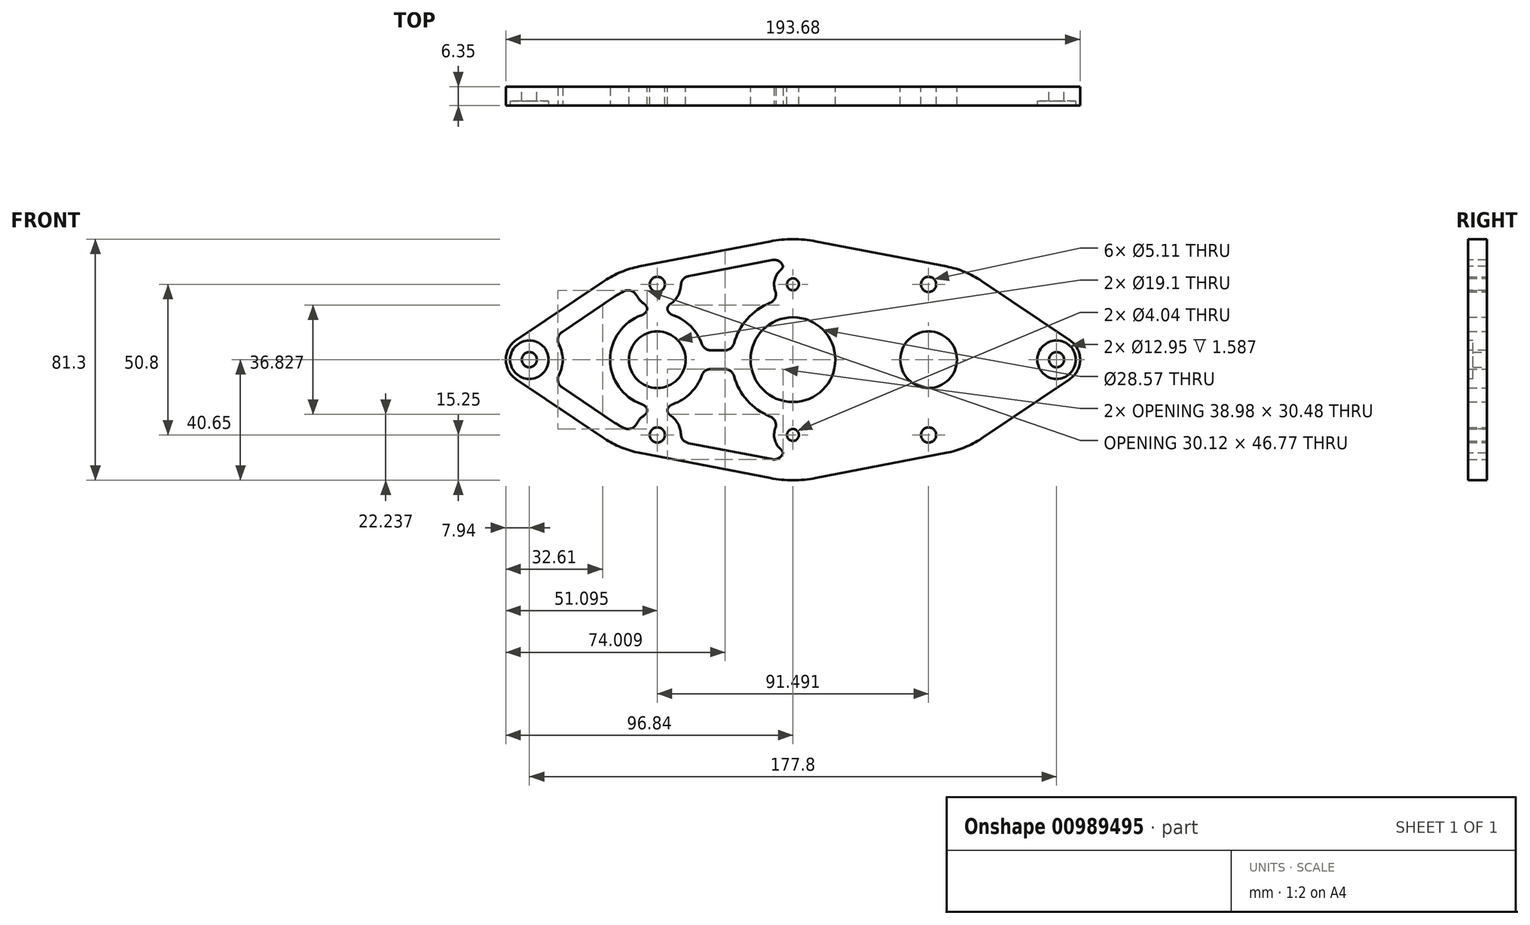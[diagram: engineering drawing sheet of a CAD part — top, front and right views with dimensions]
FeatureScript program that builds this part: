
annotation { "Feature Type Name" : "Feature", "Feature Type Description" : "" }
export const myFeature = defineFeature(function(context is Context, id is Id, definition is map)
    precondition{}
    {
        {
            var Q0;
            Q0=qCreatedBy(makeId("Front.planeOp"),FACE);
            var sketch = newSketch(context, id + "F0", { "sketchPlane" : qUnion([Q0])});
            skCircle(sketch, "E0", {"center": v(-45.75, 0) * mm, "radius": 32 * mm, "construction": true});
            skCircle(sketch, "E1", {"center": v(45.75, 0) * mm, "radius": 32 * mm, "construction": true});
            skLineSegment(sketch, "E2.bottom", {"start": v(-127, -25.4) * mm, "end": v(127, -25.4) * mm, "construction": true});
            skLineSegment(sketch, "E2.top", {"start": v(-127, 25.4) * mm, "end": v(127, 25.4) * mm, "construction": true});
            skLineSegment(sketch, "E2.left", {"start": v(-127, -25.4) * mm, "end": v(-127, 25.4) * mm, "construction": true});
            skLineSegment(sketch, "E2.right", {"start": v(127, -25.4) * mm, "end": v(127, 25.4) * mm, "construction": true});
            skPoint(sketch, "E2.middle", {"position": v(0, 0) * mm});
            skCircle(sketch, "E3", {"center": v(0, 0) * mm, "radius": 50.8 * mm, "construction": true});
            skPoint(sketch, "E3.centerSnap0", {"position": v(0, -25.4) * mm});
            skLineSegment(sketch, "E4", {"start": v(0, 0) * mm, "end": v(0, 0) * mm});
            skLineSegment(sketch, "E5", {"start": v(-45.75, 0) * mm, "end": v(45.75, 0) * mm, "construction": true});
            skCircle(sketch, "E6", {"center": v(-45.75, 0) * mm, "radius": 7.63 * mm, "construction": true});
            skCircle(sketch, "E7", {"center": v(0, 0) * mm, "radius": 38.11 * mm, "construction": true});
            skCircle(sketch, "E8", {"center": v(0, 0) * mm, "radius": 40.65 * mm, "construction": true});
            skCircle(sketch, "E9", {"center": v(-45.75, 0) * mm, "radius": 9.55 * mm});
            skCircle(sketch, "E10", {"center": v(45.75, 0) * mm, "radius": 9.55 * mm});
            skCircle(sketch, "E11", {"center": v(-114.3, 12.7) * mm, "radius": 2.55 * mm, "construction": true});
            skCircle(sketch, "E12.0.1.0", {"center": v(-114.3, -12.7) * mm, "radius": 2.55 * mm, "construction": true});
            skCircle(sketch, "E12.1.0.0", {"center": v(-88.9, 12.7) * mm, "radius": 2.55 * mm, "construction": true});
            skCircle(sketch, "E12.1.1.0", {"center": v(-88.9, -12.7) * mm, "radius": 2.55 * mm, "construction": true});
            skCircle(sketch, "E12.2.0.0", {"center": v(-63.5, 12.7) * mm, "radius": 2.55 * mm, "construction": true});
            skCircle(sketch, "E12.2.1.0", {"center": v(-63.5, -12.7) * mm, "radius": 2.55 * mm, "construction": true});
            skCircle(sketch, "E12.3.0.0", {"center": v(-38.1, 12.7) * mm, "radius": 2.55 * mm, "construction": true});
            skCircle(sketch, "E12.3.1.0", {"center": v(-38.1, -12.7) * mm, "radius": 2.55 * mm, "construction": true});
            skCircle(sketch, "E12.4.0.0", {"center": v(-12.7, 12.7) * mm, "radius": 2.55 * mm, "construction": true});
            skCircle(sketch, "E12.4.1.0", {"center": v(-12.7, -12.7) * mm, "radius": 2.55 * mm, "construction": true});
            skCircle(sketch, "E12.5.0.0", {"center": v(12.7, 12.7) * mm, "radius": 2.55 * mm, "construction": true});
            skCircle(sketch, "E12.5.1.0", {"center": v(12.7, -12.7) * mm, "radius": 2.55 * mm, "construction": true});
            skCircle(sketch, "E12.6.0.0", {"center": v(38.1, 12.7) * mm, "radius": 2.55 * mm, "construction": true});
            skCircle(sketch, "E12.6.1.0", {"center": v(38.1, -12.7) * mm, "radius": 2.55 * mm, "construction": true});
            skCircle(sketch, "E12.7.0.0", {"center": v(63.5, 12.7) * mm, "radius": 2.55 * mm, "construction": true});
            skCircle(sketch, "E12.7.1.0", {"center": v(63.5, -12.7) * mm, "radius": 2.55 * mm, "construction": true});
            skCircle(sketch, "E12.8.0.0", {"center": v(88.9, 12.7) * mm, "radius": 2.55 * mm, "construction": true});
            skCircle(sketch, "E12.8.1.0", {"center": v(88.9, -12.7) * mm, "radius": 2.55 * mm, "construction": true});
            skCircle(sketch, "E12.9.0.0", {"center": v(114.3, 12.7) * mm, "radius": 2.55 * mm, "construction": true});
            skCircle(sketch, "E12.9.1.0", {"center": v(114.3, -12.7) * mm, "radius": 2.55 * mm, "construction": true});
            skLineSegment(sketch, "E12.direction1", {"start": v(-114.3, 12.7) * mm, "end": v(-88.9, 12.7) * mm, "construction": true});
            skLineSegment(sketch, "E12.direction2", {"start": v(-114.3, 12.7) * mm, "end": v(-114.3, -12.7) * mm, "construction": true});
            skLineSegment(sketch, "E13", {"start": v(-45.75, -25.4) * mm, "end": v(-45.75, 0) * mm, "construction": true});
            skLineSegment(sketch, "E14", {"start": v(-45.75, 0) * mm, "end": v(-45.75, 25.4) * mm, "construction": true});
            skCircle(sketch, "E15", {"center": v(-45.75, 25.4) * mm, "radius": 2.55 * mm});
            skCircle(sketch, "E16", {"center": v(-45.75, -25.4) * mm, "radius": 2.55 * mm});
            skCircle(sketch, "E17.MirrorC", {"center": v(45.75, -25.4) * mm, "radius": 2.55 * mm});
            skLineSegment(sketch, "E18.MirrorCS", {"start": v(45.75, -25.4) * mm, "end": v(45.75, 0) * mm, "construction": true});
            skLineSegment(sketch, "E19.MirrorCS", {"start": v(45.75, 0) * mm, "end": v(45.75, 25.4) * mm, "construction": true});
            skCircle(sketch, "E20.MirrorC", {"center": v(45.75, 25.4) * mm, "radius": 2.55 * mm});
            skCircle(sketch, "E21", {"center": v(0, 0) * mm, "radius": 14.29 * mm});
            skCircle(sketch, "E22", {"center": v(0, 0) * mm, "radius": 15.88 * mm, "construction": true});
            skCircle(sketch, "E23", {"center": v(45.75, 0) * mm, "radius": 7.63 * mm, "construction": true});
            skArc(sketch, "E24", {"start": v(-7.69, 39.92) * mm, "mid": v(0, 40.65) * mm, "end": v(7.69, 39.92) * mm});
            skLineSegment(sketch, "E25", {"start": v(-7.69, 39.92) * mm, "end": v(-51.8, 31.43) * mm});
            skLineSegment(sketch, "E26", {"start": v(7.69, 39.92) * mm, "end": v(51.8, 31.43) * mm});
            skCircle(sketch, "E27", {"center": v(0, 0) * mm, "radius": 18.29 * mm, "construction": true});
            skCircle(sketch, "E28", {"center": v(-88.9, 0) * mm, "radius": 2.55 * mm});
            skCircle(sketch, "E29", {"center": v(88.9, 0) * mm, "radius": 2.55 * mm});
            skCircle(sketch, "E30", {"center": v(88.9, 0) * mm, "radius": 7.94 * mm, "construction": true});
            skCircle(sketch, "E31", {"center": v(-88.9, 0) * mm, "radius": 7.94 * mm, "construction": true});
            skLineSegment(sketch, "E32", {"start": v(63.6, 26.57) * mm, "end": v(93.33, 6.59) * mm});
            skArc(sketch, "E33", {"start": v(51.8, 31.43) * mm, "mid": v(57.94, 29.59) * mm, "end": v(63.6, 26.57) * mm});
            skArc(sketch, "E34", {"start": v(93.33, 6.59) * mm, "mid": v(96.84, 0) * mm, "end": v(93.33, -6.59) * mm});
            skArc(sketch, "E35", {"start": v(51.8, -31.43) * mm, "mid": v(57.94, -29.59) * mm, "end": v(63.6, -26.57) * mm});
            skLineSegment(sketch, "E36", {"start": v(63.6, -26.57) * mm, "end": v(93.33, -6.59) * mm});
            skArc(sketch, "E37", {"start": v(-93.33, 6.59) * mm, "mid": v(-96.84, 0) * mm, "end": v(-93.33, -6.59) * mm});
            skLineSegment(sketch, "E38", {"start": v(-93.33, -6.59) * mm, "end": v(-63.6, -26.57) * mm});
            skArc(sketch, "E39", {"start": v(-63.6, -26.57) * mm, "mid": v(-57.94, -29.59) * mm, "end": v(-51.8, -31.43) * mm});
            skArc(sketch, "E40", {"start": v(-51.8, 31.43) * mm, "mid": v(-57.94, 29.59) * mm, "end": v(-63.6, 26.57) * mm});
            skLineSegment(sketch, "E41", {"start": v(-63.6, 26.57) * mm, "end": v(-93.33, 6.59) * mm});
            skArc(sketch, "E42", {"start": v(-7.69, -39.92) * mm, "mid": v(0, -40.65) * mm, "end": v(7.69, -39.92) * mm});
            skLineSegment(sketch, "E43", {"start": v(7.69, -39.92) * mm, "end": v(51.8, -31.43) * mm});
            skLineSegment(sketch, "E44", {"start": v(-7.69, -39.92) * mm, "end": v(-51.8, -31.43) * mm});
            skCircle(sketch, "E45", {"center": v(0, 25.4) * mm, "radius": 2.02 * mm});
            skPoint(sketch, "E45.centerSnap0", {"position": v(0, 25.4) * mm});
            skCircle(sketch, "E46", {"center": v(0, -25.4) * mm, "radius": 2.02 * mm});
            skSolve(sketch);
        }
        {
            var Q0;
            Q0 = qSketchRegion(id + "F0", true);
            extrude(context, id + "F1", {"entities" : qUnion([Q0]), "depth" : 6.35 * mm, "offsetDistance" : 25.4 * mm});
        }
        {
            var Q0;
            Q0=makeQuery(id+"F1.opExtrude","CAP_FACE",FACE,{"disambiguationData":[OSD([sQuery(id+"F0.wireOp",EDGE,"E9"),sQuery(id+"F0.wireOp",EDGE,"E10"),sQuery(id+"F0.wireOp",EDGE,"E15"),sQuery(id+"F0.wireOp",EDGE,"E16"),sQuery(id+"F0.wireOp",EDGE,"E17.MirrorC"),sQuery(id+"F0.wireOp",EDGE,"E20.MirrorC"),sQuery(id+"F0.wireOp",EDGE,"E21"),sQuery(id+"F0.wireOp",EDGE,"E24"),sQuery(id+"F0.wireOp",EDGE,"E25"),sQuery(id+"F0.wireOp",EDGE,"E26"),sQuery(id+"F0.wireOp",EDGE,"E28"),sQuery(id+"F0.wireOp",EDGE,"E29"),sQuery(id+"F0.wireOp",EDGE,"E32"),sQuery(id+"F0.wireOp",EDGE,"E33"),sQuery(id+"F0.wireOp",EDGE,"E34"),sQuery(id+"F0.wireOp",EDGE,"E35"),sQuery(id+"F0.wireOp",EDGE,"E36"),sQuery(id+"F0.wireOp",EDGE,"E37"),sQuery(id+"F0.wireOp",EDGE,"E38"),sQuery(id+"F0.wireOp",EDGE,"E39"),sQuery(id+"F0.wireOp",EDGE,"E40"),sQuery(id+"F0.wireOp",EDGE,"E41"),sQuery(id+"F0.wireOp",EDGE,"E42"),sQuery(id+"F0.wireOp",EDGE,"E43"),sQuery(id+"F0.wireOp",EDGE,"E44")])],"isStart":false});
            var sketch = newSketch(context, id + "F2", { "sketchPlane" : qUnion([Q0])});
            skCircle(sketch, "E47", {"center": v(-88.9, 0) * mm, "radius": 6.48 * mm});
            skCircle(sketch, "E48", {"center": v(88.9, 0) * mm, "radius": 6.48 * mm});
            skSolve(sketch);
        }
        {
            var Q0;
            Q0 = qSketchRegion(id + "F2", true);
            extrude(context, id + "F3", {"entities" : qUnion([Q0]), "operationType" : NewBodyOperationType.REMOVE, "oppositeDirection" : true, "depth" : 1.59 * mm, "offsetDistance" : 25.4 * mm});
        }
        {
            var Q0;
            Q0=makeQuery(id+"F1.opExtrude","CAP_FACE",FACE,{"disambiguationData":[OSD([sQuery(id+"F0.wireOp",EDGE,"E9"),sQuery(id+"F0.wireOp",EDGE,"E10"),sQuery(id+"F0.wireOp",EDGE,"E15"),sQuery(id+"F0.wireOp",EDGE,"E16"),sQuery(id+"F0.wireOp",EDGE,"E17.MirrorC"),sQuery(id+"F0.wireOp",EDGE,"E20.MirrorC"),sQuery(id+"F0.wireOp",EDGE,"E21"),sQuery(id+"F0.wireOp",EDGE,"E24"),sQuery(id+"F0.wireOp",EDGE,"E25"),sQuery(id+"F0.wireOp",EDGE,"E26"),sQuery(id+"F0.wireOp",EDGE,"E28"),sQuery(id+"F0.wireOp",EDGE,"E29"),sQuery(id+"F0.wireOp",EDGE,"E32"),sQuery(id+"F0.wireOp",EDGE,"E33"),sQuery(id+"F0.wireOp",EDGE,"E34"),sQuery(id+"F0.wireOp",EDGE,"E35"),sQuery(id+"F0.wireOp",EDGE,"E36"),sQuery(id+"F0.wireOp",EDGE,"E37"),sQuery(id+"F0.wireOp",EDGE,"E38"),sQuery(id+"F0.wireOp",EDGE,"E39"),sQuery(id+"F0.wireOp",EDGE,"E40"),sQuery(id+"F0.wireOp",EDGE,"E41"),sQuery(id+"F0.wireOp",EDGE,"E42"),sQuery(id+"F0.wireOp",EDGE,"E43"),sQuery(id+"F0.wireOp",EDGE,"E44")])],"isStart":false});
            var sketch = newSketch(context, id + "F4", { "sketchPlane" : qUnion([Q0])});
            skCircle(sketch, "E49", {"center": v(-45.75, 25.4) * mm, "radius": 7.94 * mm, "construction": true});
            skCircle(sketch, "E50", {"center": v(-45.75, -25.4) * mm, "radius": 7.94 * mm, "construction": true});
            skCircle(sketch, "E51", {"center": v(45.75, -25.4) * mm, "radius": 7.94 * mm, "construction": true});
            skCircle(sketch, "E52", {"center": v(45.75, 25.4) * mm, "radius": 7.94 * mm, "construction": true});
            skLineSegment(sketch, "E53.0", {"start": v(-6.49, 33.68) * mm, "end": v(-50.6, 25.2) * mm, "construction": true});
            skArc(sketch, "E53.1", {"start": v(-6.49, 33.68) * mm, "mid": v(0, 34.3) * mm, "end": v(6.49, 33.68) * mm, "construction": true});
            skLineSegment(sketch, "E53.2", {"start": v(6.49, 33.68) * mm, "end": v(50.6, 25.2) * mm, "construction": true});
            skArc(sketch, "E53.3", {"start": v(50.6, 25.2) * mm, "mid": v(55.52, 23.72) * mm, "end": v(60.05, 21.3) * mm, "construction": true});
            skLineSegment(sketch, "E53.4", {"start": v(60.05, 21.3) * mm, "end": v(89.79, 1.32) * mm, "construction": true});
            skArc(sketch, "E53.5", {"start": v(-60.05, -21.3) * mm, "mid": v(-55.52, -23.72) * mm, "end": v(-50.6, -25.2) * mm, "construction": true});
            skLineSegment(sketch, "E53.6", {"start": v(-89.79, -1.32) * mm, "end": v(-60.05, -21.3) * mm, "construction": true});
            skArc(sketch, "E53.7", {"start": v(-89.79, 1.32) * mm, "mid": v(-90.49, 0) * mm, "end": v(-89.79, -1.32) * mm, "construction": true});
            skLineSegment(sketch, "E53.8", {"start": v(-60.05, 21.3) * mm, "end": v(-89.79, 1.32) * mm, "construction": true});
            skLineSegment(sketch, "E53.9", {"start": v(-6.49, -33.68) * mm, "end": v(-50.6, -25.2) * mm, "construction": true});
            skArc(sketch, "E53.10", {"start": v(-6.49, -33.68) * mm, "mid": v(0, -34.3) * mm, "end": v(6.49, -33.68) * mm, "construction": true});
            skLineSegment(sketch, "E53.11", {"start": v(6.49, -33.68) * mm, "end": v(50.6, -25.2) * mm, "construction": true});
            skArc(sketch, "E53.12", {"start": v(50.6, -25.2) * mm, "mid": v(55.52, -23.72) * mm, "end": v(60.05, -21.3) * mm, "construction": true});
            skLineSegment(sketch, "E53.13", {"start": v(60.05, -21.3) * mm, "end": v(89.79, -1.32) * mm, "construction": true});
            skArc(sketch, "E53.14", {"start": v(-50.6, 25.2) * mm, "mid": v(-55.52, 23.72) * mm, "end": v(-60.05, 21.3) * mm, "construction": true});
            skArc(sketch, "E53.15", {"start": v(89.79, 1.32) * mm, "mid": v(90.49, 0) * mm, "end": v(89.79, -1.32) * mm, "construction": true});
            skCircle(sketch, "E54", {"center": v(0, 0) * mm, "radius": 20.64 * mm, "construction": true});
            skCircle(sketch, "E55", {"center": v(-45.75, 0) * mm, "radius": 15.9 * mm, "construction": true});
            skCircle(sketch, "E56", {"center": v(45.75, 0) * mm, "radius": 15.9 * mm, "construction": true});
            skLineSegment(sketch, "E57", {"start": v(-45.75, -25.4) * mm, "end": v(-45.75, 25.4) * mm, "construction": true});
            skLineSegment(sketch, "E58", {"start": v(45.75, 25.4) * mm, "end": v(45.75, -25.4) * mm, "construction": true});
            skLineSegment(sketch, "E59", {"start": v(45.75, 0) * mm, "end": v(-45.75, 0) * mm, "construction": true});
            skLineSegment(sketch, "E60", {"start": v(-42.57, 15.58) * mm, "end": v(-42.57, 18.13) * mm});
            skLineSegment(sketch, "E61", {"start": v(-42.57, -18.13) * mm, "end": v(-42.57, -15.58) * mm});
            skArc(sketch, "E62", {"start": v(-42.57, 18.13) * mm, "mid": v(-38.56, 22.02) * mm, "end": v(-38.12, 27.6) * mm});
            skArc(sketch, "E63", {"start": v(-42.57, -18.13) * mm, "mid": v(-38.56, -22.02) * mm, "end": v(-38.12, -27.6) * mm});
            skArc(sketch, "E64", {"start": v(-53.62, 24.42) * mm, "mid": v(-52.1, 20.65) * mm, "end": v(-48.92, 18.13) * mm});
            skArc(sketch, "E65", {"start": v(-48.92, 15.58) * mm, "mid": v(-61.65, 0) * mm, "end": v(-48.92, -15.58) * mm});
            skLineSegment(sketch, "E66.MirrorCS", {"start": v(-48.92, 15.58) * mm, "end": v(-48.92, 18.13) * mm});
            skLineSegment(sketch, "E67.MirrorCS", {"start": v(-48.92, -18.13) * mm, "end": v(-48.92, -15.58) * mm});
            skCircle(sketch, "E68", {"center": v(-88.9, 0) * mm, "radius": 11.24 * mm, "construction": true});
            skLineSegment(sketch, "E69", {"start": v(-80.55, 7.52) * mm, "end": v(-60.05, 21.3) * mm});
            skArc(sketch, "E70", {"start": v(-53.62, 24.42) * mm, "mid": v(-56.95, 23.08) * mm, "end": v(-60.05, 21.3) * mm});
            skArc(sketch, "E71", {"start": v(-60.05, -21.3) * mm, "mid": v(-56.95, -23.08) * mm, "end": v(-53.62, -24.42) * mm});
            skArc(sketch, "E72", {"start": v(-48.92, -18.13) * mm, "mid": v(-52.1, -20.65) * mm, "end": v(-53.62, -24.42) * mm});
            skLineSegment(sketch, "E73", {"start": v(-60.05, -21.3) * mm, "end": v(-80.55, -7.52) * mm});
            skArc(sketch, "E74", {"start": v(-80.55, -7.52) * mm, "mid": v(-77.66, 0) * mm, "end": v(-80.55, 7.52) * mm});
            skLineSegment(sketch, "E75", {"start": v(-38.12, 27.6) * mm, "end": v(-6.49, 33.68) * mm});
            skArc(sketch, "E76", {"start": v(-3.17, 34.16) * mm, "mid": v(-4.84, 33.96) * mm, "end": v(-6.49, 33.68) * mm});
            skLineSegment(sketch, "E77", {"start": v(-38.12, -27.6) * mm, "end": v(-6.49, -33.68) * mm});
            skLineSegment(sketch, "E78", {"start": v(-6.49, -33.68) * mm, "end": v(-6.49, -33.68) * mm});
            skArc(sketch, "E79", {"start": v(-6.49, -33.68) * mm, "mid": v(-4.84, -33.96) * mm, "end": v(-3.18, -34.16) * mm});
            skLineSegment(sketch, "E80", {"start": v(-30.17, -3.18) * mm, "end": v(-20.4, -3.18) * mm});
            skLineSegment(sketch, "E81", {"start": v(-30.17, 3.18) * mm, "end": v(-20.4, 3.18) * mm});
            skArc(sketch, "E82", {"start": v(-30.17, 3.18) * mm, "mid": v(-34.5, 11.24) * mm, "end": v(-42.57, 15.58) * mm});
            skArc(sketch, "E83", {"start": v(-42.57, -15.58) * mm, "mid": v(-34.5, -11.24) * mm, "end": v(-30.17, -3.18) * mm});
            skArc(sketch, "E84", {"start": v(-20.4, -3.18) * mm, "mid": v(-16.17, -12.82) * mm, "end": v(-7.74, -19.13) * mm});
            skArc(sketch, "E85", {"start": v(-7.74, 19.13) * mm, "mid": v(-16.17, 12.82) * mm, "end": v(-20.4, 3.18) * mm});
            skCircle(sketch, "E86", {"center": v(0, 25.4) * mm, "radius": 6.35 * mm, "construction": true});
            skCircle(sketch, "E87", {"center": v(0, -25.4) * mm, "radius": 6.35 * mm, "construction": true});
            skLineSegment(sketch, "E88", {"start": v(-3.18, -34.16) * mm, "end": v(-3.18, -30.9) * mm});
            skArc(sketch, "E89", {"start": v(-3.17, -30.9) * mm, "mid": v(-5.98, -27.55) * mm, "end": v(-5.95, -23.18) * mm});
            skLineSegment(sketch, "E90", {"start": v(-3.18, 30.9) * mm, "end": v(-3.18, 34.16) * mm});
            skArc(sketch, "E91", {"start": v(-3.18, 30.9) * mm, "mid": v(-5.98, 27.55) * mm, "end": v(-5.95, 23.18) * mm});
            skArc(sketch, "E92", {"start": v(-5.95, -23.18) * mm, "mid": v(-6.02, -20.8) * mm, "end": v(-7.74, -19.13) * mm});
            skArc(sketch, "E93", {"start": v(-7.74, 19.13) * mm, "mid": v(-6.02, 20.8) * mm, "end": v(-5.95, 23.18) * mm});
            skSolve(sketch);
        }
        {
            var Q0;
            Q0 = qSketchRegion(id + "F4", true);
            extrude(context, id + "F5", {"entities" : qUnion([Q0]), "operationType" : NewBodyOperationType.REMOVE, "oppositeDirection" : true, "depth" : 25.4 * mm, "offsetDistance" : 25.4 * mm});
        }
        {
            var Q0;
            Q0=makeQuery(id+"F5.boolean.opBoolean","COPY",EDGE,{"derivedFrom":makeQuery(id+"F5.opExtrude","SWEPT_EDGE",EDGE,{"disambiguationData":[OSD([sQuery(id+"F4.wireOp",EDGE,"E69"),sQuery(id+"F4.wireOp",EDGE,"E74")])]})});
            var Q1;
            Q1=makeQuery(id+"F5.boolean.opBoolean","COPY",EDGE,{"derivedFrom":makeQuery(id+"F5.opExtrude","SWEPT_EDGE",EDGE,{"disambiguationData":[OSD([sQuery(id+"F4.wireOp",EDGE,"E73"),sQuery(id+"F4.wireOp",EDGE,"E74")])]})});
            var Q2;
            Q2=makeQuery(id+"F5.boolean.opBoolean","COPY",EDGE,{"derivedFrom":makeQuery(id+"F5.opExtrude","SWEPT_EDGE",EDGE,{"disambiguationData":[OSD([sQuery(id+"F4.wireOp",EDGE,"E71"),sQuery(id+"F4.wireOp",EDGE,"E72")])]})});
            var Q3;
            Q3=makeQuery(id+"F5.boolean.opBoolean","COPY",EDGE,{"derivedFrom":makeQuery(id+"F5.opExtrude","SWEPT_EDGE",EDGE,{"disambiguationData":[OSD([sQuery(id+"F4.wireOp",EDGE,"E67.MirrorCS"),sQuery(id+"F4.wireOp",EDGE,"E72")])]})});
            var Q4;
            Q4=makeQuery(id+"F5.boolean.opBoolean","COPY",EDGE,{"derivedFrom":makeQuery(id+"F5.opExtrude","SWEPT_EDGE",EDGE,{"disambiguationData":[OSD([sQuery(id+"F4.wireOp",EDGE,"E65"),sQuery(id+"F4.wireOp",EDGE,"E67.MirrorCS")])]})});
            var Q5;
            Q5=makeQuery(id+"F5.boolean.opBoolean","COPY",EDGE,{"derivedFrom":makeQuery(id+"F5.opExtrude","SWEPT_EDGE",EDGE,{"disambiguationData":[OSD([sQuery(id+"F4.wireOp",EDGE,"E64"),sQuery(id+"F4.wireOp",EDGE,"E70")])]})});
            var Q6;
            Q6=makeQuery(id+"F5.boolean.opBoolean","COPY",EDGE,{"derivedFrom":makeQuery(id+"F5.opExtrude","SWEPT_EDGE",EDGE,{"disambiguationData":[OSD([sQuery(id+"F4.wireOp",EDGE,"E64"),sQuery(id+"F4.wireOp",EDGE,"E66.MirrorCS")])]})});
            var Q7;
            Q7=makeQuery(id+"F5.boolean.opBoolean","COPY",EDGE,{"derivedFrom":makeQuery(id+"F5.opExtrude","SWEPT_EDGE",EDGE,{"disambiguationData":[OSD([sQuery(id+"F4.wireOp",EDGE,"E65"),sQuery(id+"F4.wireOp",EDGE,"E66.MirrorCS")])]})});
            var Q8;
            Q8=makeQuery(id+"F5.boolean.opBoolean","COPY",EDGE,{"derivedFrom":makeQuery(id+"F5.opExtrude","SWEPT_EDGE",EDGE,{"disambiguationData":[OSD([sQuery(id+"F4.wireOp",EDGE,"E81"),sQuery(id+"F4.wireOp",EDGE,"E82")])]})});
            var Q9;
            Q9=makeQuery(id+"F5.boolean.opBoolean","COPY",EDGE,{"derivedFrom":makeQuery(id+"F5.opExtrude","SWEPT_EDGE",EDGE,{"disambiguationData":[OSD([sQuery(id+"F4.wireOp",EDGE,"E60"),sQuery(id+"F4.wireOp",EDGE,"E82")])]})});
            var Q10;
            Q10=makeQuery(id+"F5.boolean.opBoolean","COPY",EDGE,{"derivedFrom":makeQuery(id+"F5.opExtrude","SWEPT_EDGE",EDGE,{"disambiguationData":[OSD([sQuery(id+"F4.wireOp",EDGE,"E60"),sQuery(id+"F4.wireOp",EDGE,"E62")])]})});
            var Q11;
            Q11=makeQuery(id+"F5.boolean.opBoolean","COPY",EDGE,{"derivedFrom":makeQuery(id+"F5.opExtrude","SWEPT_EDGE",EDGE,{"disambiguationData":[OSD([sQuery(id+"F4.wireOp",EDGE,"E62"),sQuery(id+"F4.wireOp",EDGE,"E75")])]})});
            var Q12;
            Q12=makeQuery(id+"F5.boolean.opBoolean","COPY",EDGE,{"derivedFrom":makeQuery(id+"F5.opExtrude","SWEPT_EDGE",EDGE,{"disambiguationData":[OSD([sQuery(id+"F4.wireOp",EDGE,"OSvW8WGB-dVns-i7Bp-5mNW-JiuYIDBc75Vi"),sQuery(id+"F4.wireOp",EDGE,"E76")])]})});
            var Q13;
            Q13=makeQuery(id+"F5.boolean.opBoolean","COPY",EDGE,{"derivedFrom":makeQuery(id+"F5.opExtrude","SWEPT_EDGE",EDGE,{"disambiguationData":[OSD([sQuery(id+"F4.wireOp",EDGE,"OSvW8WGB-dVns-i7Bp-5mNW-JiuYIDBc75Vi"),sQuery(id+"F4.wireOp",EDGE,"E85")])]})});
            var Q14;
            Q14=makeQuery(id+"F5.boolean.opBoolean","COPY",EDGE,{"derivedFrom":makeQuery(id+"F5.opExtrude","SWEPT_EDGE",EDGE,{"disambiguationData":[OSD([sQuery(id+"F4.wireOp",EDGE,"E81"),sQuery(id+"F4.wireOp",EDGE,"E85")])]})});
            var Q15;
            Q15=makeQuery(id+"F5.boolean.opBoolean","COPY",EDGE,{"derivedFrom":makeQuery(id+"F5.opExtrude","SWEPT_EDGE",EDGE,{"disambiguationData":[OSD([sQuery(id+"F4.wireOp",EDGE,"E80"),sQuery(id+"F4.wireOp",EDGE,"E84")])]})});
            var Q16;
            Q16=makeQuery(id+"F5.boolean.opBoolean","COPY",EDGE,{"derivedFrom":makeQuery(id+"F5.opExtrude","SWEPT_EDGE",EDGE,{"disambiguationData":[OSD([sQuery(id+"F4.wireOp",EDGE,"E80"),sQuery(id+"F4.wireOp",EDGE,"E83")])]})});
            var Q17;
            Q17=makeQuery(id+"F5.boolean.opBoolean","COPY",EDGE,{"derivedFrom":makeQuery(id+"F5.opExtrude","SWEPT_EDGE",EDGE,{"disambiguationData":[OSD([sQuery(id+"F4.wireOp",EDGE,"E61"),sQuery(id+"F4.wireOp",EDGE,"E83")])]})});
            var Q18;
            Q18=makeQuery(id+"F5.boolean.opBoolean","COPY",EDGE,{"derivedFrom":makeQuery(id+"F5.opExtrude","SWEPT_EDGE",EDGE,{"disambiguationData":[OSD([sQuery(id+"F4.wireOp",EDGE,"E61"),sQuery(id+"F4.wireOp",EDGE,"E63")])]})});
            var Q19;
            Q19=makeQuery(id+"F5.boolean.opBoolean","COPY",EDGE,{"derivedFrom":makeQuery(id+"F5.opExtrude","SWEPT_EDGE",EDGE,{"disambiguationData":[OSD([sQuery(id+"F4.wireOp",EDGE,"E63"),sQuery(id+"F4.wireOp",EDGE,"E77")])]})});
            var Q20;
            Q20=makeQuery(id+"F5.boolean.opBoolean","COPY",EDGE,{"derivedFrom":makeQuery(id+"F5.opExtrude","SWEPT_EDGE",EDGE,{"disambiguationData":[OSD([sQuery(id+"F4.wireOp",EDGE,"HjrqI1Rt-0mhT-fvh4-SzY0-CyESTQDnE33K"),sQuery(id+"F4.wireOp",EDGE,"E84")])]})});
            var Q21;
            Q21=makeQuery(id+"F5.boolean.opBoolean","COPY",EDGE,{"derivedFrom":makeQuery(id+"F5.opExtrude","SWEPT_EDGE",EDGE,{"disambiguationData":[OSD([sQuery(id+"F4.wireOp",EDGE,"E79"),sQuery(id+"F4.wireOp",EDGE,"HjrqI1Rt-0mhT-fvh4-SzY0-CyESTQDnE33K")])]})});
            var Q22;
            Q22=makeQuery(id+"F5.boolean.opBoolean","COPY",EDGE,{"derivedFrom":makeQuery(id+"F5.opExtrude","SWEPT_EDGE",EDGE,{"disambiguationData":[OSD([sQuery(id+"F4.wireOp",EDGE,"E90"),sQuery(id+"F4.wireOp",EDGE,"E91")])]})});
            var Q23;
            Q23=makeQuery(id+"F5.boolean.opBoolean","COPY",EDGE,{"derivedFrom":makeQuery(id+"F5.opExtrude","SWEPT_EDGE",EDGE,{"disambiguationData":[OSD([sQuery(id+"F4.wireOp",EDGE,"E88"),sQuery(id+"F4.wireOp",EDGE,"E89")])]})});
            fillet(context, id + "F6", {"entities" : qUnion([Q0, Q1, Q2, Q3, Q4, Q5, Q6, Q7, Q8, Q9, Q10, Q11, Q12, Q13, Q14, Q15, Q16, Q17, Q18, Q19, Q20, Q21, Q22, Q23]), "radius" : 3.17 * mm, "tangentPropagation" : true, "allowEdgeOverflow" : false});
        }
        {
            var Q0;
            {var subQ0=sQuery(id+"F4.wireOp",EDGE,"E66.MirrorCS");Q0=makeQuery(id+"F6.opFillet","BLEND_EDGE",EDGE,{"blendedFrom":[makeQuery(id+"F5.boolean.opBoolean","COPY",EDGE,{"derivedFrom":makeQuery(id+"F5.opExtrude","SWEPT_EDGE",EDGE,{"disambiguationData":[OSD([sQuery(id+"F4.wireOp",EDGE,"E64"),subQ0])]})}),makeQuery(id+"F5.boolean.opBoolean","COPY",EDGE,{"derivedFrom":makeQuery(id+"F5.opExtrude","SWEPT_EDGE",EDGE,{"disambiguationData":[OSD([sQuery(id+"F4.wireOp",EDGE,"E65"),subQ0])]})})],"blendedInto":[]});}
            var Q1;
            {var subQ0=sQuery(id+"F4.wireOp",EDGE,"E67.MirrorCS");Q1=makeQuery(id+"F6.opFillet","BLEND_EDGE",EDGE,{"blendedFrom":[makeQuery(id+"F5.boolean.opBoolean","COPY",EDGE,{"derivedFrom":makeQuery(id+"F5.opExtrude","SWEPT_EDGE",EDGE,{"disambiguationData":[OSD([sQuery(id+"F4.wireOp",EDGE,"E65"),subQ0])]})}),makeQuery(id+"F5.boolean.opBoolean","COPY",EDGE,{"derivedFrom":makeQuery(id+"F5.opExtrude","SWEPT_EDGE",EDGE,{"disambiguationData":[OSD([subQ0,sQuery(id+"F4.wireOp",EDGE,"E72")])]})})],"blendedInto":[]});}
            var Q2;
            {var subQ0=sQuery(id+"F4.wireOp",EDGE,"E60");Q2=makeQuery(id+"F6.opFillet","BLEND_EDGE",EDGE,{"blendedFrom":[makeQuery(id+"F5.boolean.opBoolean","COPY",EDGE,{"derivedFrom":makeQuery(id+"F5.opExtrude","SWEPT_EDGE",EDGE,{"disambiguationData":[OSD([subQ0,sQuery(id+"F4.wireOp",EDGE,"E82")])]})}),makeQuery(id+"F5.boolean.opBoolean","COPY",EDGE,{"derivedFrom":makeQuery(id+"F5.opExtrude","SWEPT_EDGE",EDGE,{"disambiguationData":[OSD([subQ0,sQuery(id+"F4.wireOp",EDGE,"E62")])]})})],"blendedInto":[]});}
            var Q3;
            {var subQ0=sQuery(id+"F4.wireOp",EDGE,"E61");Q3=makeQuery(id+"F6.opFillet","BLEND_EDGE",EDGE,{"blendedFrom":[makeQuery(id+"F5.boolean.opBoolean","COPY",EDGE,{"derivedFrom":makeQuery(id+"F5.opExtrude","SWEPT_EDGE",EDGE,{"disambiguationData":[OSD([subQ0,sQuery(id+"F4.wireOp",EDGE,"E63")])]})}),makeQuery(id+"F5.boolean.opBoolean","COPY",EDGE,{"derivedFrom":makeQuery(id+"F5.opExtrude","SWEPT_EDGE",EDGE,{"disambiguationData":[OSD([subQ0,sQuery(id+"F4.wireOp",EDGE,"E83")])]})})],"blendedInto":[]});}
            fillet(context, id + "F7", {"entities" : qUnion([Q0, Q1, Q2, Q3]), "radius" : 1.59 * mm, "tangentPropagation" : true, "allowEdgeOverflow" : false});
        }
    });
